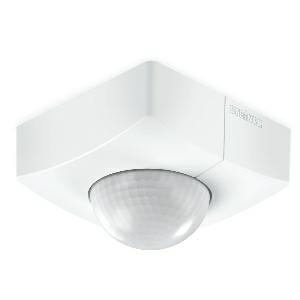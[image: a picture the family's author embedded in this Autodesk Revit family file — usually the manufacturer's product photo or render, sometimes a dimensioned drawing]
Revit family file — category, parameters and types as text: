
# Revit family: is_3360_057237
name_source: partatom
category: Elektroinstallationen
revit_build: Autodesk Revit 2016 (Build: 20190508_0715(x64)
units: mm (PartAtom-declared; Revit-internal decimal feet)

## family parameters
Basisbauteil = Fläche
Beim Laden mit Abzugskörper schneiden = Nein
Bemaßung runder Anschluss = Durchmesser verwenden
Beschriftungsausrichtung beibehalten = Nein
Gemeinsam genutzt = Nein
Raumberechnungspunkt = Nein
Teiletyp = Normal

## types (1)
- IS 3360
    Apparent Load = 0 VA
    Beschreibung = Type: Motion detectors; Dimensions (L x W x H): 65 x 95 x 95 mm; Mains power supply: 12 – 22,5 V / 50 – 60 Hz; Sensor Technology: passive infrared; Application, place: Outdoors, Indoors; Application, room: production facilities, recreation room, changing room, function room / ancillary room, sports hall, reception / lobby, stairwell, WC / washroom, multi-storey / underground car park, outdoors, warehouse, Indoors; Installation site: ceiling; Installation: Surface wiring; Switching zones: 448 switching zones; Electronic scalability: No; Mechanical scalability: No; Mounting height: 2,5 – 4,00 m; Optimum mounting height: 2,8 m; Detection angle: 360 °; Angle of aperture: 45 °; Sneak-by guard: Yes; Capability of masking out individual segments: Yes; Reach, radial: Ø 8 m (50 m²); Reach, tangential: Ø 40 m (1257 m²); Reach, presence: Ø 3 m (7 m²); Twilight setting TEACH: Yes; Twilight setting: 2 – 1000 lx; Switching output 1, floating: No; Control output, Dali: Addressable/slave; Basic light level function: No; With bus coupling: Yes; Settings via: Bus; With remote control: No; Interconnection: Yes; IP-rating: IP54; Material: Plastic; Ambient temperature: -20 – 50 °C; Colour: white; Colour, RAL: 9003; Manufacturer's Warranty: 5 years; Version: DALI-2 IPD - surface, sq.; PU1, EAN: 4007841057237
    Height = 95 mm
    Hersteller = Steinel
    Length = 65 mm
    ModVariant = Nein
    Modell = 057237
    Mounting Place = Ceiling
    Mounting Type = Surface mounted
    Number of Poles = 1
    OnlyDefault = Ja
    Power Factor = 1
    Product Name = IS 3360
    Product group = Sensor-switched outdoor light
    ProductGroupID = 3
    Protection Class = Protection class
    Protection Degree = IP 54
    RlxData = <blob elided: 60049 chars, md5=24854e2b>
    SensorDataFile = <blob elided: 5495 chars, md5=c347bae7>
    Typenbild = produkt1_057237.jpg
    Typenkommentare = Product without accessories
    URL = http://relux.com
    VarID = ---
    Voltage = 0 V
    Vorgabe-Ansicht = 1800 mm
    Weight = 0.00 kg
    Width = 95 mm

## geometry (parser evidence)
native form markers: Sweep x11
no freeform markers — native parametric forms only
